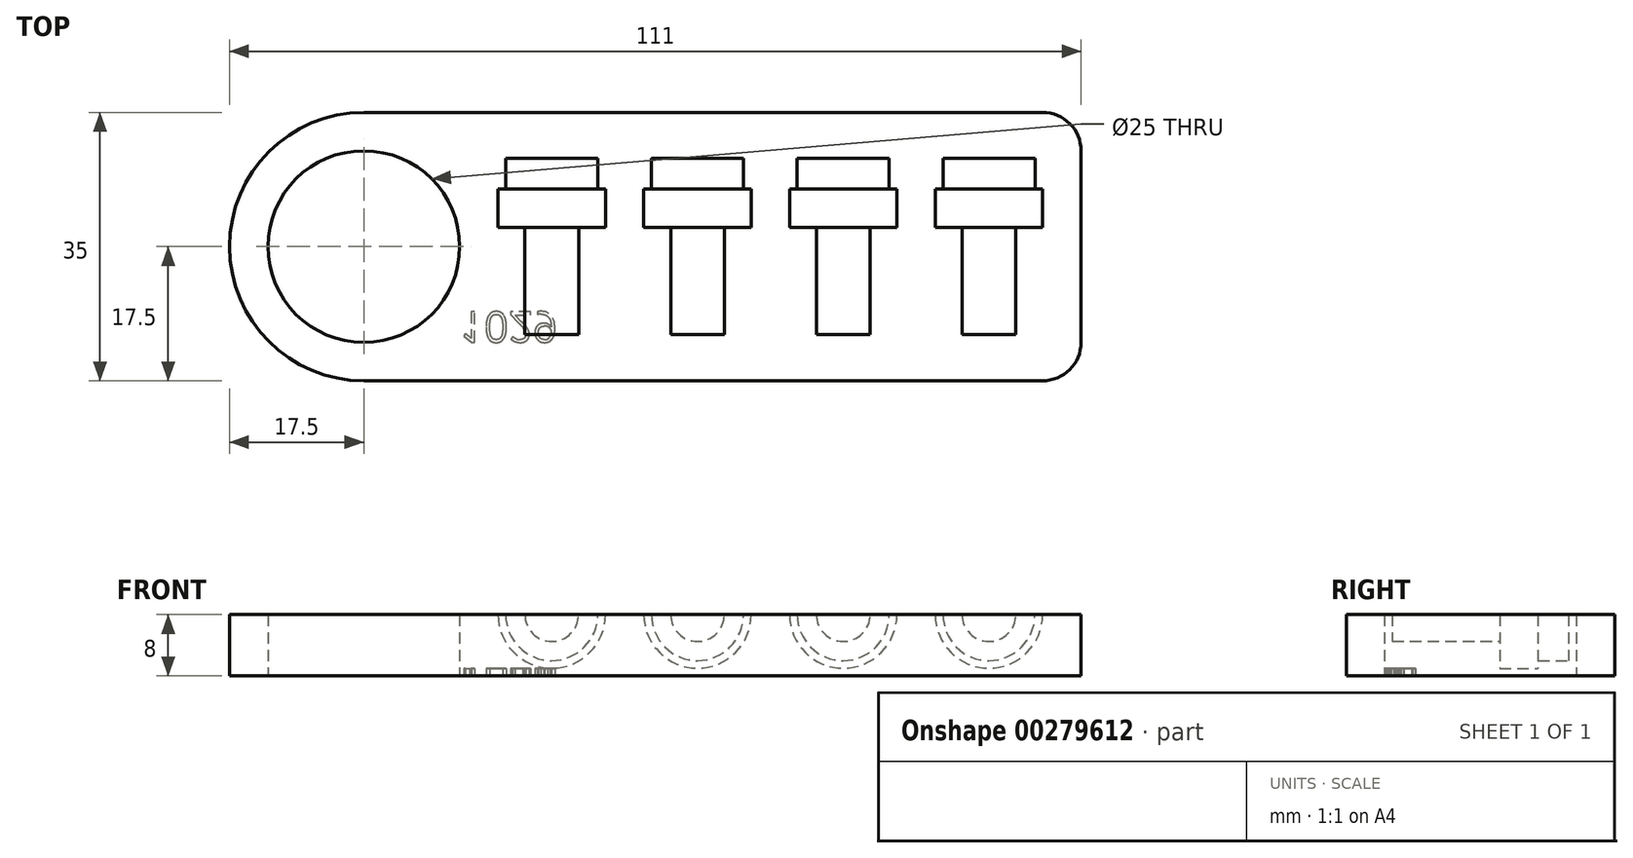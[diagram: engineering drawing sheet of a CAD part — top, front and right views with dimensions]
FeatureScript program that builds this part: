
annotation { "Feature Type Name" : "Feature", "Feature Type Description" : "" }
export const myFeature = defineFeature(function(context is Context, id is Id, definition is map)
    precondition{}
    {
        {
            var Q0;
            Q0=qCreatedBy(makeId("Top.planeOp"),FACE);
            var sketch = newSketch(context, id + "F0", { "sketchPlane" : qUnion([Q0])});
            skLineSegment(sketch, "E0.bottom", {"start": v(17.5, 0) * mm, "end": v(106, 0) * mm});
            skLineSegment(sketch, "E0.top", {"start": v(17.5, 35) * mm, "end": v(106, 35) * mm});
            skLineSegment(sketch, "E0.left", {"start": v(0, 17.5) * mm, "end": v(0, 17.5) * mm});
            skLineSegment(sketch, "E0.right", {"start": v(111, 5) * mm, "end": v(111, 30) * mm});
            skLineSegment(sketch, "E1.bottom", {"start": v(0, 0) * mm, "end": v(17.5, 0) * mm, "construction": true});
            skLineSegment(sketch, "E1.top", {"start": v(0, 17.5) * mm, "end": v(17.5, 17.5) * mm, "construction": true});
            skLineSegment(sketch, "E1.left", {"start": v(0, 0) * mm, "end": v(0, 17.5) * mm, "construction": true});
            skLineSegment(sketch, "E1.right", {"start": v(17.5, 0) * mm, "end": v(17.5, 17.5) * mm, "construction": true});
            skCircle(sketch, "E2", {"center": v(17.5, 17.5) * mm, "radius": 12.5 * mm});
            skPoint(sketch, "E3.visualSharp", {"position": v(0, 0) * mm});
            skArc(sketch, "E3.filletArc", {"start": v(0, 17.5) * mm, "mid": v(5.13, 5.13) * mm, "end": v(17.5, 0) * mm});
            skPoint(sketch, "E4.visualSharp", {"position": v(0, 35) * mm});
            skArc(sketch, "E4.filletArc", {"start": v(17.5, 35) * mm, "mid": v(5.13, 29.87) * mm, "end": v(0, 17.5) * mm});
            skPoint(sketch, "E5.visualSharp", {"position": v(111, 35) * mm});
            skArc(sketch, "E5.filletArc", {"start": v(111, 30) * mm, "mid": v(109.54, 33.54) * mm, "end": v(106, 35) * mm});
            skPoint(sketch, "E6.visualSharp", {"position": v(111, 0) * mm});
            skArc(sketch, "E6.filletArc", {"start": v(106, 0) * mm, "mid": v(109.54, 1.46) * mm, "end": v(111, 5) * mm});
            skSolve(sketch);
        }
        {
            var Q0;
            Q0=makeQuery(id+"F0.imprint","IMPRINT",FACE,{"disambiguationData":[TD([[makeQuery(id+"F0.imprint","IMPRINT",EDGE,{"derivedFrom":sQuery(id+"F0.wireOp",EDGE,"E0.bottom")}),1.0]])]});
            extrude(context, id + "F1", {"entities" : qUnion([Q0]), "depth" : 8 * mm});
        }
        {
            var Q0;
            Q0=makeQuery(id+"F1.opExtrude","CAP_FACE",FACE,{"disambiguationData":[OSD([sQuery(id+"F0.wireOp",EDGE,"E0.bottom"),sQuery(id+"F0.wireOp",EDGE,"E0.top"),sQuery(id+"F0.wireOp",EDGE,"E0.right"),sQuery(id+"F0.wireOp",EDGE,"E2"),sQuery(id+"F0.wireOp",EDGE,"E3.filletArc"),sQuery(id+"F0.wireOp",EDGE,"E4.filletArc"),sQuery(id+"F0.wireOp",EDGE,"E5.filletArc"),sQuery(id+"F0.wireOp",EDGE,"E6.filletArc")])],"isStart":false});
            var sketch = newSketch(context, id + "F2", { "sketchPlane" : qUnion([Q0])});
            skLineSegment(sketch, "E7.bottom", {"start": v(0, 0) * mm, "end": v(42, 0) * mm, "construction": true});
            skLineSegment(sketch, "E7.top", {"start": v(0, 6) * mm, "end": v(42, 6) * mm, "construction": true});
            skLineSegment(sketch, "E7.left", {"start": v(0, 0) * mm, "end": v(0, 6) * mm, "construction": true});
            skLineSegment(sketch, "E7.right", {"start": v(42, 0) * mm, "end": v(42, 6) * mm, "construction": true});
            skLineSegment(sketch, "E8", {"start": v(42, 6) * mm, "end": v(61, 6) * mm, "construction": true});
            skLineSegment(sketch, "E9", {"start": v(61, 6) * mm, "end": v(80, 6) * mm, "construction": true});
            skLineSegment(sketch, "E10", {"start": v(80, 6) * mm, "end": v(99, 6) * mm, "construction": true});
            skLineSegment(sketch, "E11.bottom", {"start": v(42, 6) * mm, "end": v(45.5, 6) * mm});
            skLineSegment(sketch, "E11.left", {"start": v(42, 6) * mm, "end": v(42, 20) * mm});
            skLineSegment(sketch, "E11.right", {"start": v(45.5, 6) * mm, "end": v(45.5, 20) * mm});
            skLineSegment(sketch, "E12.bottom", {"start": v(45.5, 20) * mm, "end": v(49, 20) * mm});
            skLineSegment(sketch, "E12.top", {"start": v(48, 25) * mm, "end": v(49, 25) * mm});
            skLineSegment(sketch, "E12.left", {"start": v(42, 20) * mm, "end": v(42, 25) * mm});
            skLineSegment(sketch, "E12.right", {"start": v(49, 20) * mm, "end": v(49, 25) * mm});
            skLineSegment(sketch, "E13.top", {"start": v(42, 29) * mm, "end": v(48, 29) * mm});
            skLineSegment(sketch, "E13.left", {"start": v(42, 25) * mm, "end": v(42, 29) * mm});
            skLineSegment(sketch, "E13.right", {"start": v(48, 25) * mm, "end": v(48, 29) * mm});
            skLineSegment(sketch, "E14.bottom", {"start": v(61, 6) * mm, "end": v(64.5, 6) * mm});
            skLineSegment(sketch, "E14.left", {"start": v(61, 6) * mm, "end": v(61, 20) * mm});
            skLineSegment(sketch, "E14.right", {"start": v(64.5, 6) * mm, "end": v(64.5, 20) * mm});
            skLineSegment(sketch, "E15.bottom", {"start": v(64.5, 20) * mm, "end": v(68, 20) * mm});
            skLineSegment(sketch, "E15.top", {"start": v(67, 25) * mm, "end": v(68, 25) * mm});
            skLineSegment(sketch, "E15.left", {"start": v(61, 20) * mm, "end": v(61, 25) * mm});
            skLineSegment(sketch, "E15.right", {"start": v(68, 20) * mm, "end": v(68, 25) * mm});
            skLineSegment(sketch, "E16.top", {"start": v(61, 29) * mm, "end": v(67, 29) * mm});
            skLineSegment(sketch, "E16.left", {"start": v(61, 25) * mm, "end": v(61, 29) * mm});
            skLineSegment(sketch, "E16.right", {"start": v(67, 25) * mm, "end": v(67, 29) * mm});
            skLineSegment(sketch, "E17.bottom", {"start": v(80, 6) * mm, "end": v(83.5, 6) * mm});
            skLineSegment(sketch, "E17.left", {"start": v(80, 6) * mm, "end": v(80, 20) * mm});
            skLineSegment(sketch, "E17.right", {"start": v(83.5, 6) * mm, "end": v(83.5, 20) * mm});
            skLineSegment(sketch, "E18.bottom", {"start": v(83.5, 20) * mm, "end": v(87, 20) * mm});
            skLineSegment(sketch, "E18.top", {"start": v(86, 25) * mm, "end": v(87, 25) * mm});
            skLineSegment(sketch, "E18.left", {"start": v(80, 20) * mm, "end": v(80, 25) * mm});
            skLineSegment(sketch, "E18.right", {"start": v(87, 20) * mm, "end": v(87, 25) * mm});
            skLineSegment(sketch, "E19.top", {"start": v(80, 29) * mm, "end": v(86, 29) * mm});
            skLineSegment(sketch, "E19.left", {"start": v(80, 25) * mm, "end": v(80, 29) * mm});
            skLineSegment(sketch, "E19.right", {"start": v(86, 25) * mm, "end": v(86, 29) * mm});
            skLineSegment(sketch, "E20.bottom", {"start": v(99, 6) * mm, "end": v(102.5, 6) * mm});
            skLineSegment(sketch, "E20.left", {"start": v(99, 6) * mm, "end": v(99, 20) * mm});
            skLineSegment(sketch, "E20.right", {"start": v(102.5, 6) * mm, "end": v(102.5, 20) * mm});
            skLineSegment(sketch, "E21.bottom", {"start": v(102.5, 20) * mm, "end": v(106, 20) * mm});
            skLineSegment(sketch, "E21.top", {"start": v(105, 25) * mm, "end": v(106, 25) * mm});
            skLineSegment(sketch, "E21.left", {"start": v(99, 20) * mm, "end": v(99, 25) * mm});
            skLineSegment(sketch, "E21.right", {"start": v(106, 20) * mm, "end": v(106, 25) * mm});
            skLineSegment(sketch, "E22.top", {"start": v(99, 29) * mm, "end": v(105, 29) * mm});
            skLineSegment(sketch, "E22.left", {"start": v(99, 25) * mm, "end": v(99, 29) * mm});
            skLineSegment(sketch, "E22.right", {"start": v(105, 25) * mm, "end": v(105, 29) * mm});
            skSolve(sketch);
        }
        {
            var Q0;
            Q0=makeQuery(id+"F2.imprint","IMPRINT",FACE,{"disambiguationData":[TD([[makeQuery(id+"F2.imprint","IMPRINT",EDGE,{"derivedFrom":sQuery(id+"F2.wireOp",EDGE,"E11.bottom")}),1.0]])]});
            var Q1;
            Q1=sQuery(id+"F2.wireOp",EDGE,"E12.left");
            revolve(context, id + "F3", {"operationType" : NewBodyOperationType.REMOVE, "entities" : qUnion([Q0]), "axis" : qUnion([Q1]), "revolveType" : RevolveType.FULL, "oppositeDirection" : true});
        }
        {
            var Q0;
            Q0=makeQuery(id+"F2.imprint","IMPRINT",FACE,{"disambiguationData":[TD([[makeQuery(id+"F2.imprint","IMPRINT",EDGE,{"derivedFrom":sQuery(id+"F2.wireOp",EDGE,"E14.bottom")}),1.0]])]});
            var Q1;
            Q1=sQuery(id+"F2.wireOp",EDGE,"E15.left");
            revolve(context, id + "F4", {"operationType" : NewBodyOperationType.REMOVE, "entities" : qUnion([Q0]), "axis" : qUnion([Q1]), "revolveType" : RevolveType.FULL, "oppositeDirection" : true});
        }
        {
            var Q0;
            Q0=makeQuery(id+"F2.imprint","IMPRINT",FACE,{"disambiguationData":[TD([[makeQuery(id+"F2.imprint","IMPRINT",EDGE,{"derivedFrom":sQuery(id+"F2.wireOp",EDGE,"E17.bottom")}),1.0]])]});
            var Q1;
            Q1=sQuery(id+"F2.wireOp",EDGE,"E17.left");
            revolve(context, id + "F5", {"operationType" : NewBodyOperationType.REMOVE, "entities" : qUnion([Q0]), "axis" : qUnion([Q1]), "revolveType" : RevolveType.FULL, "oppositeDirection" : true});
        }
        {
            var Q0;
            Q0=makeQuery(id+"F2.imprint","IMPRINT",FACE,{"disambiguationData":[TD([[makeQuery(id+"F2.imprint","IMPRINT",EDGE,{"derivedFrom":sQuery(id+"F2.wireOp",EDGE,"E20.bottom")}),1.0]])]});
            var Q1;
            Q1=sQuery(id+"F2.wireOp",EDGE,"E20.left");
            revolve(context, id + "F6", {"operationType" : NewBodyOperationType.REMOVE, "entities" : qUnion([Q0]), "axis" : qUnion([Q1]), "revolveType" : RevolveType.FULL, "oppositeDirection" : true});
        }
        {
            var Q0;
            Q0=makeQuery(id+"F1.opExtrude","CAP_FACE",FACE,{"disambiguationData":[OSD([sQuery(id+"F0.wireOp",EDGE,"E0.bottom"),sQuery(id+"F0.wireOp",EDGE,"E0.top"),sQuery(id+"F0.wireOp",EDGE,"E0.right"),sQuery(id+"F0.wireOp",EDGE,"E2"),sQuery(id+"F0.wireOp",EDGE,"E3.filletArc"),sQuery(id+"F0.wireOp",EDGE,"E4.filletArc"),sQuery(id+"F0.wireOp",EDGE,"E5.filletArc"),sQuery(id+"F0.wireOp",EDGE,"E6.filletArc")])],"isStart":true});
            var sketch = newSketch(context, id + "F7", { "sketchPlane" : qUnion([Q0])});
            skLineSegment(sketch, "E23.bottom", {"start": v(0, 0) * mm, "end": v(30, 0) * mm, "construction": true});
            skLineSegment(sketch, "E23.top", {"start": v(0, -5) * mm, "end": v(30, -5) * mm, "construction": true});
            skLineSegment(sketch, "E23.left", {"start": v(0, 0) * mm, "end": v(0, -5) * mm, "construction": true});
            skLineSegment(sketch, "E23.right", {"start": v(30, 0) * mm, "end": v(30, -5) * mm, "construction": true});
            skText(sketch, "E24", { "text": "1029", "fontName": "OpenSans-Regular.ttf"});
            const initialGuessF7  = {"E24": [0.03, -0.009, 1, 0, 0.004]};
            skSetInitialGuess(sketch, initialGuessF7);
            skSolve(sketch);
        }
        {
            var Q0;
            Q0 = qSketchRegion(id + "F7", true);
            extrude(context, id + "F8", {"entities" : qUnion([Q0]), "operationType" : NewBodyOperationType.REMOVE, "oppositeDirection" : true, "depth" : 1 * mm});
        }
    });
